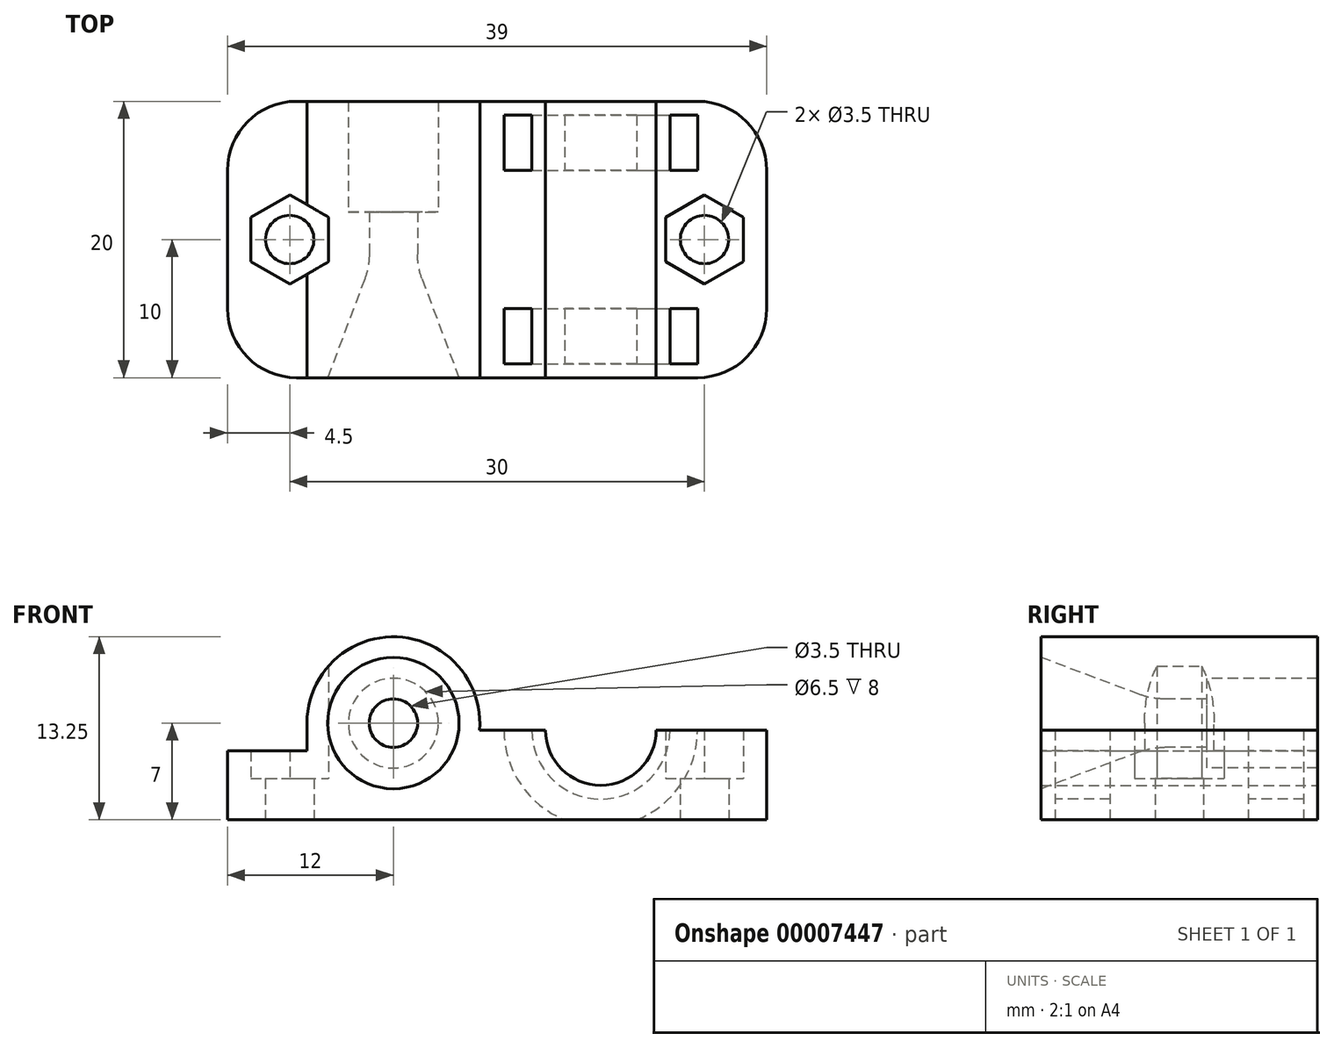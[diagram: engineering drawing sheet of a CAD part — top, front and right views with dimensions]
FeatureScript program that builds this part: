
annotation { "Feature Type Name" : "Feature", "Feature Type Description" : "" }
export const myFeature = defineFeature(function(context is Context, id is Id, definition is map)
    precondition{}
    {
        {
            var Q0;
            Q0=qCreatedBy(makeId("Front.planeOp"),FACE);
            var sketch = newSketch(context, id + "F0", { "sketchPlane" : qUnion([Q0])});
            skLineSegment(sketch, "E0", {"start": v(0, 0) * mm, "end": v(39, 0) * mm});
            skLineSegment(sketch, "E1", {"start": v(39, 0) * mm, "end": v(39, 6.5) * mm});
            skLineSegment(sketch, "E2", {"start": v(0, 5) * mm, "end": v(0, 0) * mm});
            skCircle(sketch, "E3", {"center": v(12, 7) * mm, "radius": 3.25 * mm});
            skCircle(sketch, "E4", {"center": v(27, 6.5) * mm, "radius": 4 * mm});
            skCircle(sketch, "E5", {"center": v(12, 7) * mm, "radius": 6.25 * mm});
            skLineSegment(sketch, "E6", {"start": v(0, 5) * mm, "end": v(5.75, 5) * mm});
            skLineSegment(sketch, "E7", {"start": v(5.75, 5) * mm, "end": v(5.75, 7) * mm});
            skLineSegment(sketch, "E8", {"start": v(27, 6.5) * mm, "end": v(39, 6.5) * mm});
            skLineSegment(sketch, "E9", {"start": v(27, 6.5) * mm, "end": v(18.23, 6.5) * mm});
            skSolve(sketch);
        }
        {
            var Q0;
            Q0=makeQuery(id+"F0.imprint","IMPRINT",FACE,{"disambiguationData":[TD([[makeQuery(id+"F0.imprint","IMPRINT",EDGE,{"derivedFrom":sQuery(id+"F0.wireOp",EDGE,"E0")}),1.0]])]});
            var Q1;
            Q1=makeQuery(id+"F0.imprint","IMPRINT",FACE,{"disambiguationData":[TD([[makeQuery(id+"F0.imprint","IMPRINT",EDGE,{"derivedFrom":sQuery(id+"F0.wireOp",EDGE,"E3")}),-1.0]])]});
            var Q2;
            Q2=makeQuery(id+"F0.imprint","IMPRINT",FACE,{"disambiguationData":[TD([[makeQuery(id+"F0.imprint","IMPRINT",EDGE,{"derivedFrom":sQuery(id+"F0.wireOp",EDGE,"E3")}),1.0]])]});
            extrude(context, id + "F1", {"entities" : qUnion([Q0, Q1, Q2]), "depth" : 20 * mm});
        }
        {
            var Q0;
            Q0=qCreatedBy(makeId("Top.planeOp"),FACE);
            var Q1;
            Q1=sQuery(id+"F0.wireOp",VERTEX,"E5.center");
            cPlane(context, id + "F2", {"entities" : qUnion([Q0, Q1]), "cplaneType" : CPlaneType.PLANE_POINT, "offset" : 150 * mm, "width" : 150 * mm, "height" : 150 * mm});
        }
        {
            var Q0;
            Q0=qCreatedBy(id+"F2.planeOp",FACE);
            var sketch = newSketch(context, id + "F3", { "sketchPlane" : qUnion([Q0])});
            skPoint(sketch, "E10.0", {"position": v(12, 0) * mm});
            skLineSegment(sketch, "E11.0", {"start": v(15.25, 0) * mm, "end": v(8.75, 0) * mm});
            skLineSegment(sketch, "E12.0", {"start": v(18.25, -20) * mm, "end": v(5.75, -20) * mm});
            skLineSegment(sketch, "E13", {"start": v(12, 0) * mm, "end": v(12, -20) * mm});
            skLineSegment(sketch, "E14", {"start": v(16.75, -20) * mm, "end": v(13.75, -12) * mm});
            skLineSegment(sketch, "E15", {"start": v(13.75, -12) * mm, "end": v(13.75, -8) * mm});
            skLineSegment(sketch, "E16", {"start": v(13.75, -8) * mm, "end": v(15.25, -8) * mm});
            skLineSegment(sketch, "E17", {"start": v(15.25, -8) * mm, "end": v(15.25, 0) * mm});
            skSolve(sketch);
        }
        {
            var Q0;
            {var subQ2=sQuery(id+"F3.wireOp",EDGE,"E13");Q0=makeQuery(id+"F3.imprint","IMPRINT",FACE,{"disambiguationData":[TD([[makeQuery(id+"F3.imprint","IMPRINT",EDGE,{"derivedFrom":subQ2}),1.0]])]});}
            var Q1;
            Q1=sQuery(id+"F3.wireOp",EDGE,"E13");
            revolve(context, id + "F4", {"operationType" : NewBodyOperationType.REMOVE, "entities" : qUnion([Q0]), "axis" : qUnion([Q1]), "revolveType" : RevolveType.FULL, "oppositeDirection" : true});
        }
        {
            var Q0;
            Q0=makeQuery(id+"F1.opExtrude","SWEPT_FACE",FACE,{"disambiguationData":[OSD([sQuery(id+"F0.wireOp",EDGE,"E8")])]});
            var sketch = newSketch(context, id + "F5", { "sketchPlane" : qUnion([Q0])});
            skLineSegment(sketch, "E18.0", {"start": v(31, -20) * mm, "end": v(23, -20) * mm});
            skLineSegment(sketch, "E19.0.0", {"start": v(23, 0) * mm, "end": v(31, 0) * mm});
            skLineSegment(sketch, "E19.0.1", {"start": v(23, 0) * mm, "end": v(23, -20) * mm});
            skLineSegment(sketch, "E19.0.3", {"start": v(31, -20) * mm, "end": v(31, 0) * mm});
            skLineSegment(sketch, "E20", {"start": v(27, 0) * mm, "end": v(27, -20) * mm, "construction": true});
            skLineSegment(sketch, "E21.rect.bottom", {"start": v(34, -5) * mm, "end": v(32, -5) * mm});
            skLineSegment(sketch, "E21.rect.top", {"start": v(34, -1) * mm, "end": v(32, -1) * mm});
            skLineSegment(sketch, "E21.rect.left", {"start": v(34, -5) * mm, "end": v(34, -1) * mm});
            skLineSegment(sketch, "E21.rect.right", {"start": v(32, -5) * mm, "end": v(32, -1) * mm});
            skPoint(sketch, "E21.rect.middle", {"position": v(33, -3) * mm});
            skLineSegment(sketch, "E22", {"start": v(27, -10) * mm, "end": v(35.45, -10) * mm, "construction": true});
            skLineSegment(sketch, "E23.0.MirrorCS", {"start": v(34, -15) * mm, "end": v(32, -15) * mm});
            skLineSegment(sketch, "E23.1.MirrorCS", {"start": v(32, -15) * mm, "end": v(32, -19) * mm});
            skLineSegment(sketch, "E23.2.MirrorCS", {"start": v(34, -19) * mm, "end": v(32, -19) * mm});
            skLineSegment(sketch, "E23.3.MirrorCS", {"start": v(34, -15) * mm, "end": v(34, -19) * mm});
            skSolve(sketch);
        }
        {
            var Q0;
            Q0=makeQuery(id+"F5.imprint","IMPRINT",FACE,{"disambiguationData":[TD([[makeQuery(id+"F5.imprint","IMPRINT",EDGE,{"derivedFrom":sQuery(id+"F5.wireOp",EDGE,"E21.rect.bottom")}),-1.0]])]});
            var Q1;
            Q1=makeQuery(id+"F5.imprint","IMPRINT",FACE,{"disambiguationData":[TD([[makeQuery(id+"F5.imprint","IMPRINT",EDGE,{"derivedFrom":sQuery(id+"F5.wireOp",EDGE,"E23.0.MirrorCS")}),1.0]])]});
            var Q2;
            Q2=sQuery(id+"F5.wireOp",EDGE,"E20");
            revolve(context, id + "F6", {"operationType" : NewBodyOperationType.REMOVE, "entities" : qUnion([Q0, Q1]), "axis" : qUnion([Q2]), "revolveType" : RevolveType.FULL, "oppositeDirection" : true});
        }
        {
            var Q0;
            Q0=makeQuery(id+"F1.opExtrude","SWEPT_FACE",FACE,{"disambiguationData":[OSD([sQuery(id+"F0.wireOp",EDGE,"E0")])]});
            var sketch = newSketch(context, id + "F7", { "sketchPlane" : qUnion([Q0])});
            skLineSegment(sketch, "E24.0.0", {"start": v(0, 0) * mm, "end": v(39, 0) * mm, "construction": true});
            skLineSegment(sketch, "E24.0.1", {"start": v(39, 0) * mm, "end": v(39, 20) * mm, "construction": true});
            skLineSegment(sketch, "E24.0.2", {"start": v(39, 20) * mm, "end": v(0, 20) * mm, "construction": true});
            skLineSegment(sketch, "E24.0.3", {"start": v(0, 20) * mm, "end": v(0, 0) * mm, "construction": true});
            skCircle(sketch, "E25", {"center": v(4.5, 10) * mm, "radius": 1.75 * mm});
            skCircle(sketch, "E26.cCircle", {"center": v(4.5, 10) * mm, "radius": 2.8 * mm, "construction": true});
            skLineSegment(sketch, "E26.0", {"start": v(7.3, 11.62) * mm, "end": v(7.3, 8.38) * mm});
            skLineSegment(sketch, "E26.1", {"start": v(7.3, 8.38) * mm, "end": v(4.5, 6.77) * mm});
            skLineSegment(sketch, "E26.2", {"start": v(4.5, 6.77) * mm, "end": v(1.7, 8.38) * mm});
            skLineSegment(sketch, "E26.3", {"start": v(1.7, 8.38) * mm, "end": v(1.7, 11.62) * mm});
            skLineSegment(sketch, "E26.4", {"start": v(1.7, 11.62) * mm, "end": v(4.5, 13.23) * mm});
            skLineSegment(sketch, "E26.5", {"start": v(4.5, 13.23) * mm, "end": v(7.3, 11.62) * mm});
            skPoint(sketch, "E26.0.midPoint", {"position": v(7.3, 10) * mm});
            skLineSegment(sketch, "E27", {"start": v(4.5, 10) * mm, "end": v(0, 10) * mm, "construction": true});
            skLineSegment(sketch, "E28", {"start": v(4.5, 10) * mm, "end": v(34.5, 10) * mm, "construction": true});
            skCircle(sketch, "E29", {"center": v(34.5, 10) * mm, "radius": 1.75 * mm});
            skCircle(sketch, "E30.cCircle", {"center": v(34.5, 10) * mm, "radius": 2.8 * mm, "construction": true});
            skLineSegment(sketch, "E30.0", {"start": v(37.3, 11.62) * mm, "end": v(37.3, 8.38) * mm});
            skLineSegment(sketch, "E30.1", {"start": v(37.3, 8.38) * mm, "end": v(34.5, 6.77) * mm});
            skLineSegment(sketch, "E30.2", {"start": v(34.5, 6.77) * mm, "end": v(31.7, 8.38) * mm});
            skLineSegment(sketch, "E30.3", {"start": v(31.7, 8.38) * mm, "end": v(31.7, 11.62) * mm});
            skLineSegment(sketch, "E30.4", {"start": v(31.7, 11.62) * mm, "end": v(34.5, 13.23) * mm});
            skLineSegment(sketch, "E30.5", {"start": v(34.5, 13.23) * mm, "end": v(37.3, 11.62) * mm});
            skPoint(sketch, "E30.0.midPoint", {"position": v(37.3, 10) * mm});
            skLineSegment(sketch, "E31", {"start": v(19.5, 10) * mm, "end": v(19.5, 0) * mm, "construction": true});
            skSolve(sketch);
        }
        {
            var Q0;
            Q0=makeQuery(id+"F7.imprint","IMPRINT",FACE,{"disambiguationData":[TD([[makeQuery(id+"F7.imprint","IMPRINT",EDGE,{"derivedFrom":sQuery(id+"F7.wireOp",EDGE,"E25")}),-1.0]])]});
            var Q1;
            Q1=makeQuery(id+"F7.imprint","IMPRINT",FACE,{"disambiguationData":[TD([[makeQuery(id+"F7.imprint","IMPRINT",EDGE,{"derivedFrom":sQuery(id+"F7.wireOp",EDGE,"E25")}),1.0]])]});
            var Q2;
            Q2=makeQuery(id+"F7.imprint","IMPRINT",FACE,{"disambiguationData":[TD([[makeQuery(id+"F7.imprint","IMPRINT",EDGE,{"derivedFrom":sQuery(id+"F7.wireOp",EDGE,"E29")}),1.0]])]});
            var Q3;
            Q3=makeQuery(id+"F7.imprint","IMPRINT",FACE,{"disambiguationData":[TD([[makeQuery(id+"F7.imprint","IMPRINT",EDGE,{"derivedFrom":sQuery(id+"F7.wireOp",EDGE,"E29")}),-1.0]])]});
            extrude(context, id + "F8", {"entities" : qUnion([Q0, Q1, Q2, Q3]), "operationType" : NewBodyOperationType.REMOVE, "endBound" : BoundingType.THROUGH_ALL, "oppositeDirection" : true, "depth" : 25 * mm});
        }
        {
            var Q0;
            Q0=makeQuery(id+"F7.imprint","IMPRINT",FACE,{"disambiguationData":[TD([[makeQuery(id+"F7.imprint","IMPRINT",EDGE,{"derivedFrom":sQuery(id+"F7.wireOp",EDGE,"E25")}),-1.0]])]});
            var Q1;
            Q1=makeQuery(id+"F7.imprint","IMPRINT",FACE,{"disambiguationData":[TD([[makeQuery(id+"F7.imprint","IMPRINT",EDGE,{"derivedFrom":sQuery(id+"F7.wireOp",EDGE,"E29")}),-1.0]])]});
            extrude(context, id + "F9", {"entities" : qUnion([Q0, Q1]), "operationType" : NewBodyOperationType.ADD, "oppositeDirection" : true, "depth" : 3 * mm});
        }
        {
            var Q0;
            Q0=makeQuery(id+"F1.opExtrude","CAP_EDGE",EDGE,{"disambiguationData":[OSD([sQuery(id+"F0.wireOp",EDGE,"E2")])],"isStart":true});
            var Q1;
            Q1=makeQuery(id+"F1.opExtrude","CAP_EDGE",EDGE,{"disambiguationData":[OSD([sQuery(id+"F0.wireOp",EDGE,"E2")])],"isStart":false});
            var Q2;
            Q2=makeQuery(id+"F1.opExtrude","CAP_EDGE",EDGE,{"disambiguationData":[OSD([sQuery(id+"F0.wireOp",EDGE,"E1")])],"isStart":false});
            var Q3;
            Q3=makeQuery(id+"F1.opExtrude","CAP_EDGE",EDGE,{"disambiguationData":[OSD([sQuery(id+"F0.wireOp",EDGE,"E1")])],"isStart":true});
            var Q4;
            Q4=makeQuery(id+"F4.boolean.opBoolean","COPY",EDGE,{"derivedFrom":makeQuery(id+"F4.opRevolve","SWEPT_EDGE",EDGE,{"disambiguationData":[OSD([sQuery(id+"F3.wireOp",EDGE,"E14"),sQuery(id+"F3.wireOp",EDGE,"E15")])]})});
            var Q5;
            Q5=makeQuery(id+"F4.boolean.opBoolean","COPY",EDGE,{"derivedFrom":makeQuery(id+"F4.opRevolve","SWEPT_EDGE",EDGE,{"disambiguationData":[OSD([sQuery(id+"F3.wireOp",EDGE,"E12.0"),sQuery(id+"F3.wireOp",EDGE,"E14")])]})});
            fillet(context, id + "F10", {"entities" : qUnion([Q0, Q1, Q2, Q3, Q4, Q5]), "radius" : 5 * mm, "tangentPropagation" : true, "allowEdgeOverflow" : false});
        }
    });
